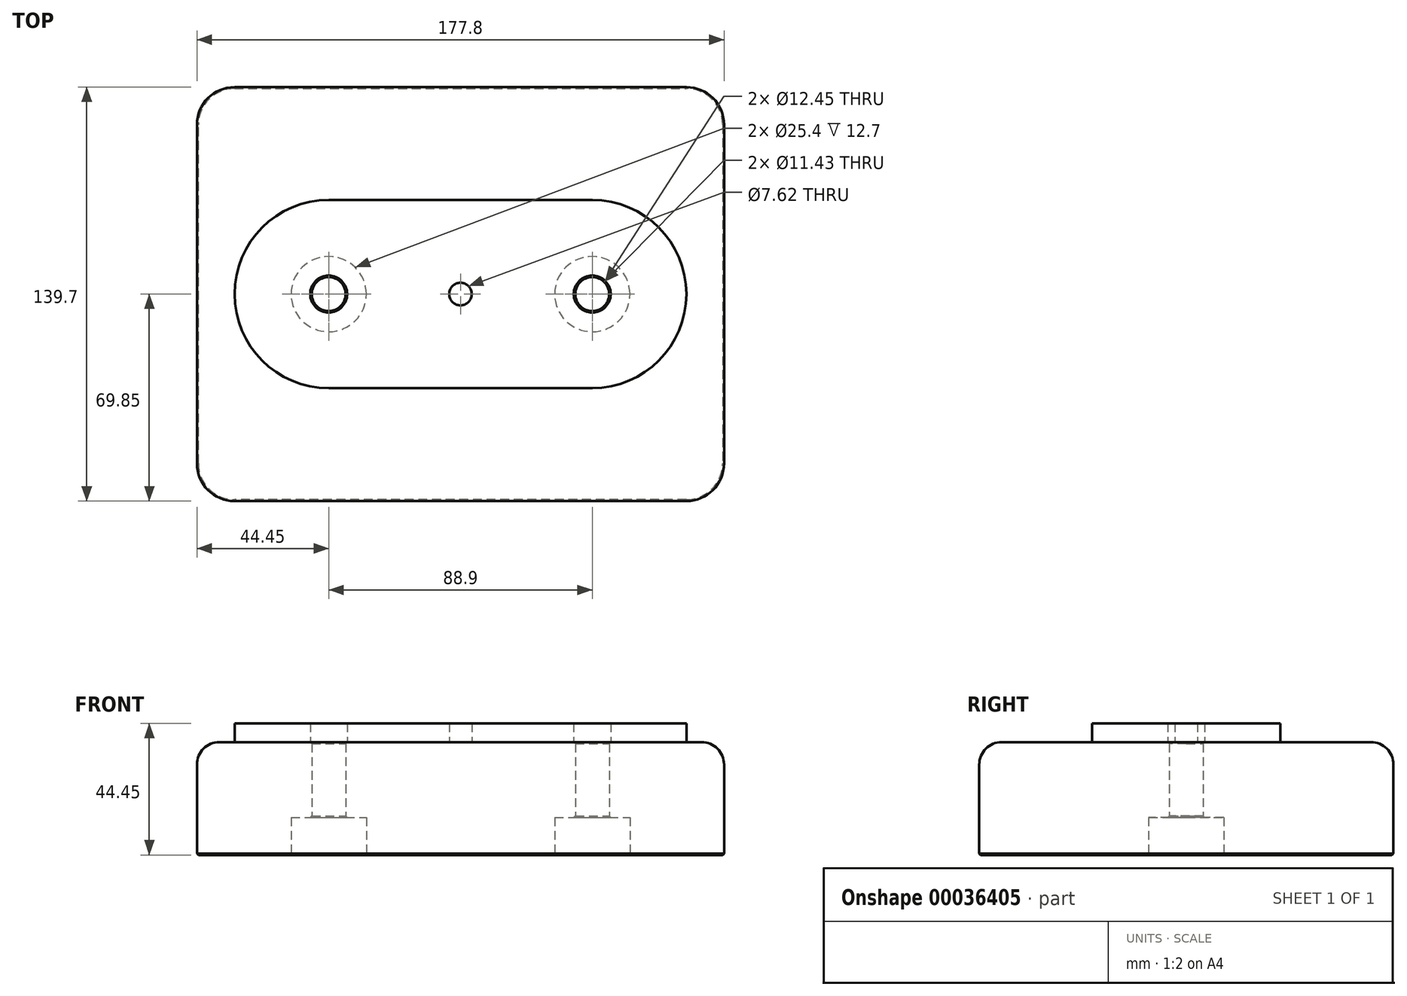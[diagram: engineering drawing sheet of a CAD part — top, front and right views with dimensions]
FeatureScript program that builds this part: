
annotation { "Feature Type Name" : "Feature", "Feature Type Description" : "" }
export const myFeature = defineFeature(function(context is Context, id is Id, definition is map)
    precondition{}
    {
        {
            var Q0;
            Q0=qCreatedBy(makeId("Top.planeOp"),FACE);
            var sketch = newSketch(context, id + "F0", { "sketchPlane" : qUnion([Q0])});
            skLineSegment(sketch, "E0.bottom", {"start": v(-76.2, 69.85) * mm, "end": v(76.2, 69.85) * mm});
            skLineSegment(sketch, "E0.top", {"start": v(-76.2, -69.85) * mm, "end": v(76.2, -69.85) * mm});
            skLineSegment(sketch, "E0.left", {"start": v(-88.9, 57.15) * mm, "end": v(-88.9, -57.15) * mm});
            skLineSegment(sketch, "E0.right", {"start": v(88.9, 57.15) * mm, "end": v(88.9, -57.15) * mm});
            skPoint(sketch, "E1.visualSharp", {"position": v(-88.9, 69.85) * mm});
            skArc(sketch, "E1.filletArc", {"start": v(-76.2, 69.85) * mm, "mid": v(-85.18, 66.13) * mm, "end": v(-88.9, 57.15) * mm});
            skPoint(sketch, "E2.visualSharp", {"position": v(88.9, 69.85) * mm});
            skArc(sketch, "E2.filletArc", {"start": v(88.9, 57.15) * mm, "mid": v(85.18, 66.13) * mm, "end": v(76.2, 69.85) * mm});
            skPoint(sketch, "E3.visualSharp", {"position": v(88.9, -69.85) * mm});
            skArc(sketch, "E3.filletArc", {"start": v(76.2, -69.85) * mm, "mid": v(85.18, -66.13) * mm, "end": v(88.9, -57.15) * mm});
            skPoint(sketch, "E4.visualSharp", {"position": v(-88.9, -69.85) * mm});
            skArc(sketch, "E4.filletArc", {"start": v(-88.9, -57.15) * mm, "mid": v(-85.18, -66.13) * mm, "end": v(-76.2, -69.85) * mm});
            skLineSegment(sketch, "E5", {"start": v(-88.9, 0) * mm, "end": v(88.9, 0) * mm, "construction": true});
            skLineSegment(sketch, "E6", {"start": v(0, 69.85) * mm, "end": v(0, -69.85) * mm, "construction": true});
            skSolve(sketch);
        }
        {
            var Q0;
            Q0=makeQuery(id+"F0.imprint","IMPRINT",FACE,{"disambiguationData":[TD([[makeQuery(id+"F0.imprint","IMPRINT",EDGE,{"derivedFrom":sQuery(id+"F0.wireOp",EDGE,"E0.bottom")}),-1.0]])]});
            extrude(context, id + "F1", {"entities" : qUnion([Q0]), "oppositeDirection" : true, "depth" : 38.1 * mm});
        }
        {
            var Q0;
            Q0=makeQuery(id+"F1.opExtrude","CAP_EDGE",EDGE,{"disambiguationData":[OSD([sQuery(id+"F0.wireOp",EDGE,"E0.top")])],"isStart":true});
            fillet(context, id + "F2", {"entities" : qUnion([Q0]), "radius" : 7.62 * mm, "tangentPropagation" : true, "allowEdgeOverflow" : false});
        }
        {
            var Q0;
            Q0=makeQuery(id+"F1.opExtrude","CAP_FACE",FACE,{"disambiguationData":[OSD([sQuery(id+"F0.wireOp",EDGE,"E0.bottom"),sQuery(id+"F0.wireOp",EDGE,"E0.top"),sQuery(id+"F0.wireOp",EDGE,"E0.left"),sQuery(id+"F0.wireOp",EDGE,"E0.right"),sQuery(id+"F0.wireOp",EDGE,"E1.filletArc"),sQuery(id+"F0.wireOp",EDGE,"E2.filletArc"),sQuery(id+"F0.wireOp",EDGE,"E3.filletArc"),sQuery(id+"F0.wireOp",EDGE,"E4.filletArc")])],"isStart":false});
            var sketch = newSketch(context, id + "F3", { "sketchPlane" : qUnion([Q0])});
            skLineSegment(sketch, "E7", {"start": v(-44.45, 0) * mm, "end": v(44.45, 0) * mm, "construction": true});
            skCircle(sketch, "E8", {"center": v(-44.45, 0) * mm, "radius": 12.7 * mm});
            skCircle(sketch, "E9", {"center": v(44.45, 0) * mm, "radius": 12.7 * mm});
            skPoint(sketch, "E10", {"position": v(0, 0) * mm});
            skCircle(sketch, "E11", {"center": v(-44.45, 0) * mm, "radius": 5.72 * mm});
            skCircle(sketch, "E12", {"center": v(44.45, 0) * mm, "radius": 5.72 * mm});
            skSolve(sketch);
        }
        {
            var Q0;
            Q0=makeQuery(id+"F3.imprint","IMPRINT",FACE,{"disambiguationData":[TD([[makeQuery(id+"F3.imprint","IMPRINT",EDGE,{"derivedFrom":sQuery(id+"F3.wireOp",EDGE,"E8")}),1.0]])]});
            var Q1;
            Q1=makeQuery(id+"F3.imprint","IMPRINT",FACE,{"disambiguationData":[TD([[makeQuery(id+"F3.imprint","IMPRINT",EDGE,{"derivedFrom":sQuery(id+"F3.wireOp",EDGE,"E11")}),1.0]])]});
            var Q2;
            Q2=makeQuery(id+"F3.imprint","IMPRINT",FACE,{"disambiguationData":[TD([[makeQuery(id+"F3.imprint","IMPRINT",EDGE,{"derivedFrom":sQuery(id+"F3.wireOp",EDGE,"E9")}),1.0]])]});
            var Q3;
            Q3=makeQuery(id+"F3.imprint","IMPRINT",FACE,{"disambiguationData":[TD([[makeQuery(id+"F3.imprint","IMPRINT",EDGE,{"derivedFrom":sQuery(id+"F3.wireOp",EDGE,"E12")}),1.0]])]});
            extrude(context, id + "F4", {"entities" : qUnion([Q0, Q1, Q2, Q3]), "operationType" : NewBodyOperationType.REMOVE, "oppositeDirection" : true, "depth" : 12.7 * mm});
        }
        {
            var Q0;
            Q0=makeQuery(id+"F3.imprint","IMPRINT",FACE,{"disambiguationData":[TD([[makeQuery(id+"F3.imprint","IMPRINT",EDGE,{"derivedFrom":sQuery(id+"F3.wireOp",EDGE,"E11")}),1.0]])]});
            var Q1;
            Q1=makeQuery(id+"F3.imprint","IMPRINT",FACE,{"disambiguationData":[TD([[makeQuery(id+"F3.imprint","IMPRINT",EDGE,{"derivedFrom":sQuery(id+"F3.wireOp",EDGE,"E12")}),1.0]])]});
            extrude(context, id + "F5", {"entities" : qUnion([Q0, Q1]), "operationType" : NewBodyOperationType.REMOVE, "endBound" : BoundingType.THROUGH_ALL, "oppositeDirection" : true, "depth" : 25.4 * mm});
        }
        {
            var Q0;
            Q0=makeQuery(id+"F1.opExtrude","CAP_EDGE",EDGE,{"disambiguationData":[OSD([sQuery(id+"F0.wireOp",EDGE,"E0.top")])],"isStart":false});
            var Q1;
            Q1=makeQuery(id+"F4.boolean.opBoolean","COPY",EDGE,{"derivedFrom":makeQuery(id+"F4.opExtrude","CAP_EDGE",EDGE,{"disambiguationData":[OSD([sQuery(id+"F3.wireOp",EDGE,"E8")])],"isStart":true})});
            var Q2;
            Q2=makeQuery(id+"F4.boolean.opBoolean","COPY",EDGE,{"derivedFrom":makeQuery(id+"F4.opExtrude","CAP_EDGE",EDGE,{"disambiguationData":[OSD([sQuery(id+"F3.wireOp",EDGE,"E9")])],"isStart":true})});
            var Q3;
            Q3=makeQuery(id+"F5.boolean.opBoolean","INTERSECT",EDGE,{"derivedFrom":[makeQuery(id+"F4.boolean.opBoolean","COPY",FACE,{"derivedFrom":makeQuery(id+"F4.opExtrude","CAP_FACE",FACE,{"disambiguationData":[OSD([sQuery(id+"F3.wireOp",EDGE,"E9")])],"isStart":false})}),makeQuery(id+"F5.opExtrude","SWEPT_FACE",FACE,{"disambiguationData":[OSD([sQuery(id+"F3.wireOp",EDGE,"E12")])]})]});
            var Q4;
            Q4=makeQuery(id+"F5.boolean.opBoolean","INTERSECT",EDGE,{"derivedFrom":[makeQuery(id+"F4.boolean.opBoolean","COPY",FACE,{"derivedFrom":makeQuery(id+"F4.opExtrude","CAP_FACE",FACE,{"disambiguationData":[OSD([sQuery(id+"F3.wireOp",EDGE,"E8")])],"isStart":false})}),makeQuery(id+"F5.opExtrude","SWEPT_FACE",FACE,{"disambiguationData":[OSD([sQuery(id+"F3.wireOp",EDGE,"E11")])]})]});
            var Q5;
            Q5=makeQuery(id+"F5.boolean.opBoolean","INTERSECT",EDGE,{"derivedFrom":[makeQuery(id+"F1.opExtrude","CAP_FACE",FACE,{"disambiguationData":[OSD([sQuery(id+"F0.wireOp",EDGE,"E0.bottom"),sQuery(id+"F0.wireOp",EDGE,"E0.top"),sQuery(id+"F0.wireOp",EDGE,"E0.left"),sQuery(id+"F0.wireOp",EDGE,"E0.right"),sQuery(id+"F0.wireOp",EDGE,"E1.filletArc"),sQuery(id+"F0.wireOp",EDGE,"E2.filletArc"),sQuery(id+"F0.wireOp",EDGE,"E3.filletArc"),sQuery(id+"F0.wireOp",EDGE,"E4.filletArc")])],"isStart":true}),makeQuery(id+"F5.opExtrude","SWEPT_FACE",FACE,{"disambiguationData":[OSD([sQuery(id+"F3.wireOp",EDGE,"E12")])]})]});
            var Q6;
            Q6=makeQuery(id+"F5.boolean.opBoolean","INTERSECT",EDGE,{"derivedFrom":[makeQuery(id+"F1.opExtrude","CAP_FACE",FACE,{"disambiguationData":[OSD([sQuery(id+"F0.wireOp",EDGE,"E0.bottom"),sQuery(id+"F0.wireOp",EDGE,"E0.top"),sQuery(id+"F0.wireOp",EDGE,"E0.left"),sQuery(id+"F0.wireOp",EDGE,"E0.right"),sQuery(id+"F0.wireOp",EDGE,"E1.filletArc"),sQuery(id+"F0.wireOp",EDGE,"E2.filletArc"),sQuery(id+"F0.wireOp",EDGE,"E3.filletArc"),sQuery(id+"F0.wireOp",EDGE,"E4.filletArc")])],"isStart":true}),makeQuery(id+"F5.opExtrude","SWEPT_FACE",FACE,{"disambiguationData":[OSD([sQuery(id+"F3.wireOp",EDGE,"E11")])]})]});
            chamfer(context, id + "F6", {"entities" : qUnion([Q0, Q1, Q2, Q3, Q4, Q5, Q6]), "width" : 0.5 * mm, "tangentPropagation" : true});
        }
        {
            var Q0;
            Q0=makeQuery(id+"F1.opExtrude","CAP_FACE",FACE,{"disambiguationData":[OSD([sQuery(id+"F0.wireOp",EDGE,"E0.bottom"),sQuery(id+"F0.wireOp",EDGE,"E0.top"),sQuery(id+"F0.wireOp",EDGE,"E0.left"),sQuery(id+"F0.wireOp",EDGE,"E0.right"),sQuery(id+"F0.wireOp",EDGE,"E1.filletArc"),sQuery(id+"F0.wireOp",EDGE,"E2.filletArc"),sQuery(id+"F0.wireOp",EDGE,"E3.filletArc"),sQuery(id+"F0.wireOp",EDGE,"E4.filletArc")])],"isStart":true});
            var sketch = newSketch(context, id + "F7", { "sketchPlane" : qUnion([Q0])});
            skLineSegment(sketch, "E13", {"start": v(-143.83, 0) * mm, "end": v(198.36, 0) * mm, "construction": true});
            skLineSegment(sketch, "E14", {"start": v(0, 106.07) * mm, "end": v(0, -104.2) * mm, "construction": true});
            skLineSegment(sketch, "E15.bottom", {"start": v(-44.45, 31.75) * mm, "end": v(44.45, 31.75) * mm});
            skLineSegment(sketch, "E15.top", {"start": v(-44.45, -31.75) * mm, "end": v(44.45, -31.75) * mm});
            skLineSegment(sketch, "E15.left", {"start": v(-76.2, 0) * mm, "end": v(-76.2, 0) * mm});
            skLineSegment(sketch, "E15.right", {"start": v(76.2, 0) * mm, "end": v(76.2, 0) * mm});
            skPoint(sketch, "E16", {"position": v(-76.2, 0) * mm});
            skPoint(sketch, "E17", {"position": v(0, 31.75) * mm});
            skPoint(sketch, "E18.visualSharp", {"position": v(-76.2, 31.75) * mm});
            skArc(sketch, "E18.filletArc", {"start": v(-44.45, 31.75) * mm, "mid": v(-66.9, 22.45) * mm, "end": v(-76.2, 0) * mm});
            skPoint(sketch, "E19.visualSharp", {"position": v(-76.2, -31.75) * mm});
            skArc(sketch, "E19.filletArc", {"start": v(-76.2, 0) * mm, "mid": v(-66.9, -22.45) * mm, "end": v(-44.45, -31.75) * mm});
            skPoint(sketch, "E20.visualSharp", {"position": v(76.2, 31.75) * mm});
            skArc(sketch, "E20.filletArc", {"start": v(76.2, 0) * mm, "mid": v(66.9, 22.45) * mm, "end": v(44.45, 31.75) * mm});
            skPoint(sketch, "E21.visualSharp", {"position": v(76.2, -31.75) * mm});
            skArc(sketch, "E21.filletArc", {"start": v(44.45, -31.75) * mm, "mid": v(66.9, -22.45) * mm, "end": v(76.2, 0) * mm});
            skCircle(sketch, "E22", {"center": v(0, 0) * mm, "radius": 3.81 * mm});
            skSolve(sketch);
        }
        {
            var Q0;
            {var subQ0=sQuery(id+"F7.wireOp",EDGE,"E19.filletArc");var subQ4=sQuery(id+"F7.wireOp",EDGE,"E18.filletArc");var subQ5=makeQuery(id+"F7.imprint","INTERSECT",VERTEX,{"derivedFrom":[subQ4,subQ0]});Q0=makeQuery(id+"F7.imprint","IMPRINT",FACE,{"disambiguationData":[TD([[makeQuery(id+"F7.imprint","IMPRINT",EDGE,{"disambiguationData":[TD([[subQ5,1.0]])],"derivedFrom":subQ4}),1.0]])]});}
            var Q1;
            {var subQ8=sQuery(id+"F7.wireOp",EDGE,"E15.bottom");Q1=makeQuery(id+"F7.imprint","IMPRINT",FACE,{"disambiguationData":[TD([[makeQuery(id+"F7.imprint","IMPRINT",EDGE,{"derivedFrom":subQ8}),-1.0]])]});}
            var Q2;
            {var subQ2=sQuery(id+"F7.wireOp",EDGE,"E21.filletArc");var subQ4=sQuery(id+"F7.wireOp",EDGE,"E20.filletArc");var subQ6=makeQuery(id+"F7.imprint","INTERSECT",VERTEX,{"derivedFrom":[subQ4,subQ2]});Q2=makeQuery(id+"F7.imprint","IMPRINT",FACE,{"disambiguationData":[TD([[makeQuery(id+"F7.imprint","IMPRINT",EDGE,{"disambiguationData":[TD([[subQ6,-1.0]])],"derivedFrom":subQ4}),1.0]])]});}
            extrude(context, id + "F8", {"entities" : qUnion([Q0, Q1, Q2]), "depth" : 6.35 * mm});
        }
    });
